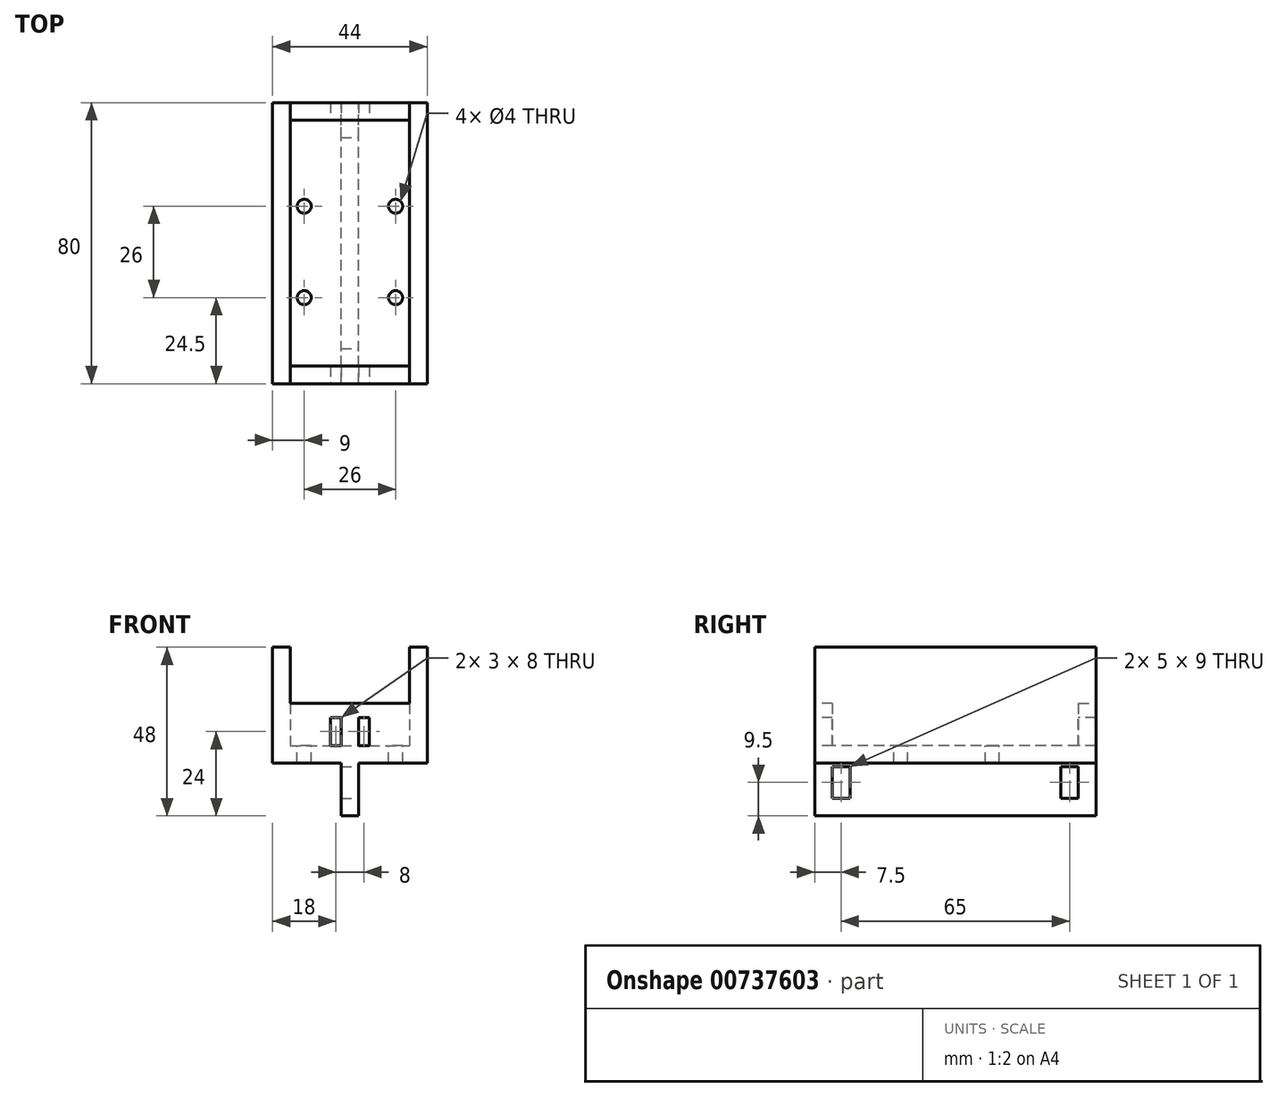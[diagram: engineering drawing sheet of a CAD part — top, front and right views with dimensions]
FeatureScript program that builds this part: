
annotation { "Feature Type Name" : "Feature", "Feature Type Description" : "" }
export const myFeature = defineFeature(function(context is Context, id is Id, definition is map)
    precondition{}
    {
        {
            var Q0;
            Q0=qCreatedBy(makeId("Top.planeOp"),FACE);
            var sketch = newSketch(context, id + "F0", { "sketchPlane" : qUnion([Q0])});
            skLineSegment(sketch, "E0.bottom", {"start": v(-13, 13) * mm, "end": v(13, 13) * mm, "construction": true});
            skLineSegment(sketch, "E0.top", {"start": v(-13, -13) * mm, "end": v(13, -13) * mm, "construction": true});
            skLineSegment(sketch, "E0.left", {"start": v(-13, 13) * mm, "end": v(-13, -13) * mm, "construction": true});
            skLineSegment(sketch, "E0.right", {"start": v(13, 13) * mm, "end": v(13, -13) * mm, "construction": true});
            skPoint(sketch, "E0.middle", {"position": v(0, 0) * mm});
            skCircle(sketch, "E1", {"center": v(-13, 13) * mm, "radius": 2 * mm});
            skCircle(sketch, "E2", {"center": v(13, 13) * mm, "radius": 2 * mm});
            skCircle(sketch, "E3", {"center": v(13, -13) * mm, "radius": 2 * mm});
            skCircle(sketch, "E4", {"center": v(-13, -13) * mm, "radius": 2 * mm});
            skLineSegment(sketch, "E5.bottom", {"start": v(-22, 37.5) * mm, "end": v(22, 37.5) * mm});
            skLineSegment(sketch, "E5.top", {"start": v(-22, -37.5) * mm, "end": v(22, -37.5) * mm});
            skLineSegment(sketch, "E5.left", {"start": v(-22, 37.5) * mm, "end": v(-22, -37.5) * mm});
            skLineSegment(sketch, "E5.right", {"start": v(22, 37.5) * mm, "end": v(22, -37.5) * mm});
            skLineSegment(sketch, "E6", {"start": v(-17, 37.5) * mm, "end": v(-17, -37.5) * mm});
            skLineSegment(sketch, "E7.MirrorCS", {"start": v(17, 37.5) * mm, "end": v(17, -37.5) * mm});
            skLineSegment(sketch, "E8", {"start": v(-17, -32.5) * mm, "end": v(17, -32.5) * mm});
            skLineSegment(sketch, "E9", {"start": v(22, 37.5) * mm, "end": v(22, 42.5) * mm});
            skLineSegment(sketch, "E10", {"start": v(22, 42.5) * mm, "end": v(-22, 42.5) * mm});
            skLineSegment(sketch, "E11", {"start": v(-22, 42.5) * mm, "end": v(-22, 37.5) * mm});
            skLineSegment(sketch, "E12", {"start": v(17, 37.5) * mm, "end": v(17, 42.5) * mm});
            skLineSegment(sketch, "E13", {"start": v(-17, 37.5) * mm, "end": v(-17, 42.5) * mm});
            skSolve(sketch);
        }
        {
            var Q0;
            {var subQ0=sQuery(id+"F0.wireOp",EDGE,"E5.left");Q0=makeQuery(id+"F0.imprint","IMPRINT",FACE,{"disambiguationData":[TD([[makeQuery(id+"F0.imprint","IMPRINT",EDGE,{"derivedFrom":subQ0}),1.0]])]});}
            var Q1;
            {var subQ0=sQuery(id+"F0.wireOp",EDGE,"E5.right");Q1=makeQuery(id+"F0.imprint","IMPRINT",FACE,{"disambiguationData":[TD([[makeQuery(id+"F0.imprint","IMPRINT",EDGE,{"derivedFrom":subQ0}),-1.0]])]});}
            extrude(context, id + "F1", {"entities" : qUnion([Q0, Q1]), "depth" : 28 * mm, "offsetDistance" : 25 * mm});
        }
        {
            var Q0;
            {var subQ0=sQuery(id+"F0.wireOp",EDGE,"E5.left");Q0=makeQuery(id+"F0.imprint","IMPRINT",FACE,{"disambiguationData":[TD([[makeQuery(id+"F0.imprint","IMPRINT",EDGE,{"derivedFrom":subQ0}),1.0]])]});}
            var Q1;
            Q1=makeQuery(id+"F0.imprint","IMPRINT",FACE,{"disambiguationData":[TD([[makeQuery(id+"F0.imprint","IMPRINT",EDGE,{"derivedFrom":sQuery(id+"F0.wireOp",EDGE,"E1")}),-1.0]])]});
            var Q2;
            {var subQ0=sQuery(id+"F0.wireOp",EDGE,"E5.right");Q2=makeQuery(id+"F0.imprint","IMPRINT",FACE,{"disambiguationData":[TD([[makeQuery(id+"F0.imprint","IMPRINT",EDGE,{"derivedFrom":subQ0}),-1.0]])]});}
            var Q3;
            {var subQ5=sQuery(id+"F0.wireOp",EDGE,"E8");Q3=makeQuery(id+"F0.imprint","IMPRINT",FACE,{"disambiguationData":[TD([[makeQuery(id+"F0.imprint","IMPRINT",EDGE,{"derivedFrom":subQ5}),-1.0]])]});}
            extrude(context, id + "F2", {"entities" : qUnion([Q0, Q1, Q2, Q3]), "operationType" : NewBodyOperationType.ADD, "oppositeDirection" : true, "depth" : 5 * mm, "offsetDistance" : 25 * mm});
        }
        {
            var Q0;
            {var subQ5=sQuery(id+"F0.wireOp",EDGE,"E8");Q0=makeQuery(id+"F0.imprint","IMPRINT",FACE,{"disambiguationData":[TD([[makeQuery(id+"F0.imprint","IMPRINT",EDGE,{"derivedFrom":subQ5}),-1.0]])]});}
            var Q1;
            Q1=makeQuery(id+"F1.opExtrude","CAP_FACE",FACE,{"disambiguationData":[OSD([sQuery(id+"F0.wireOp",EDGE,"E5.bottom"),sQuery(id+"F0.wireOp",EDGE,"E5.top"),sQuery(id+"F0.wireOp",EDGE,"E5.left"),sQuery(id+"F0.wireOp",EDGE,"E6")])],"isStart":false});
            extrude(context, id + "F3", {"entities" : qUnion([Q0]), "operationType" : NewBodyOperationType.ADD, "depth" : 12 * mm, "endBoundEntityFace" : qUnion([Q1]), "offsetDistance" : 25 * mm});
        }
        {
            var Q0;
            {var subQ0=sQuery(id+"F0.wireOp",EDGE,"E9");Q0=makeQuery(id+"F0.imprint","IMPRINT",FACE,{"disambiguationData":[TD([[makeQuery(id+"F0.imprint","IMPRINT",EDGE,{"derivedFrom":subQ0}),1.0]])]});}
            var Q1;
            {var subQ2=sQuery(id+"F0.wireOp",EDGE,"E12");Q1=makeQuery(id+"F0.imprint","IMPRINT",FACE,{"disambiguationData":[TD([[makeQuery(id+"F0.imprint","IMPRINT",EDGE,{"derivedFrom":subQ2}),1.0]])]});}
            var Q2;
            {var subQ0=sQuery(id+"F0.wireOp",EDGE,"E11");Q2=makeQuery(id+"F0.imprint","IMPRINT",FACE,{"disambiguationData":[TD([[makeQuery(id+"F0.imprint","IMPRINT",EDGE,{"derivedFrom":subQ0}),1.0]])]});}
            var Q3;
            Q3=makeQuery(id+"F2.opExtrude","CAP_FACE",FACE,{"disambiguationData":[OSD([sQuery(id+"F0.wireOp",EDGE,"E1"),sQuery(id+"F0.wireOp",EDGE,"E2"),sQuery(id+"F0.wireOp",EDGE,"E3"),sQuery(id+"F0.wireOp",EDGE,"E4"),sQuery(id+"F0.wireOp",EDGE,"E5.bottom"),sQuery(id+"F0.wireOp",EDGE,"E5.top"),sQuery(id+"F0.wireOp",EDGE,"E5.left"),sQuery(id+"F0.wireOp",EDGE,"E5.right")])],"isStart":false});
            extrude(context, id + "F4", {"entities" : qUnion([Q0, Q1, Q2]), "operationType" : NewBodyOperationType.ADD, "endBound" : BoundingType.UP_TO_SURFACE, "oppositeDirection" : true, "depth" : 25 * mm, "endBoundEntityFace" : qUnion([Q3]), "offsetDistance" : 25 * mm});
        }
        {
            var Q0;
            {var subQ0=sQuery(id+"F0.wireOp",EDGE,"E9");Q0=makeQuery(id+"F0.imprint","IMPRINT",FACE,{"disambiguationData":[TD([[makeQuery(id+"F0.imprint","IMPRINT",EDGE,{"derivedFrom":subQ0}),1.0]])]});}
            var Q1;
            {var subQ0=sQuery(id+"F0.wireOp",EDGE,"E11");Q1=makeQuery(id+"F0.imprint","IMPRINT",FACE,{"disambiguationData":[TD([[makeQuery(id+"F0.imprint","IMPRINT",EDGE,{"derivedFrom":subQ0}),1.0]])]});}
            var Q2;
            Q2=makeQuery(id+"F1.opExtrude","CAP_FACE",FACE,{"disambiguationData":[OSD([sQuery(id+"F0.wireOp",EDGE,"E5.bottom"),sQuery(id+"F0.wireOp",EDGE,"E5.top"),sQuery(id+"F0.wireOp",EDGE,"E5.right"),sQuery(id+"F0.wireOp",EDGE,"E7.MirrorCS")])],"isStart":false});
            extrude(context, id + "F5", {"entities" : qUnion([Q0, Q1]), "operationType" : NewBodyOperationType.ADD, "endBound" : BoundingType.UP_TO_SURFACE, "depth" : 25 * mm, "endBoundEntityFace" : qUnion([Q2]), "offsetDistance" : 25 * mm});
        }
        {
            var Q0;
            {var subQ2=sQuery(id+"F0.wireOp",EDGE,"E12");Q0=makeQuery(id+"F0.imprint","IMPRINT",FACE,{"disambiguationData":[TD([[makeQuery(id+"F0.imprint","IMPRINT",EDGE,{"derivedFrom":subQ2}),1.0]])]});}
            extrude(context, id + "F6", {"entities" : qUnion([Q0]), "operationType" : NewBodyOperationType.ADD, "depth" : 12 * mm, "offsetDistance" : 25 * mm});
        }
        {
            var Q0;
            {var subQ0=sQuery(id+"F0.wireOp",EDGE,"E5.right");var subQ1=sQuery(id+"F0.wireOp",EDGE,"E5.left");var subQ2=sQuery(id+"F0.wireOp",EDGE,"E5.top");var subQ3=sQuery(id+"F0.wireOp",EDGE,"E5.bottom");var subQ4=sQuery(id+"F0.wireOp",EDGE,"E4");var subQ5=sQuery(id+"F0.wireOp",EDGE,"E3");var subQ6=sQuery(id+"F0.wireOp",EDGE,"E2");var subQ7=sQuery(id+"F0.wireOp",EDGE,"E1");Q0=makeQuery(id+"F4.boolean.opBoolean","MERGE",FACE,{"derivedFrom":[makeQuery(id+"F2.opExtrude","CAP_FACE",FACE,{"disambiguationData":[OSD([subQ7,subQ6,subQ5,subQ4,subQ3,subQ2,subQ1,subQ0])],"isStart":false}),makeQuery(id+"F4.opExtrude","CAP_FACE",FACE,{"disambiguationData":[OSD([subQ7,subQ6,subQ5,subQ4,subQ3,subQ2,subQ1,subQ0])],"isStart":false})]});}
            var sketch = newSketch(context, id + "F7", { "sketchPlane" : qUnion([Q0])});
            skLineSegment(sketch, "E14", {"start": v(-2.5, 37.5) * mm, "end": v(-2.5, -42.5) * mm});
            skLineSegment(sketch, "E15", {"start": v(2.5, 37.5) * mm, "end": v(2.5, -42.5) * mm});
            skSolve(sketch);
        }
        {
            var Q0;
            {var subQ0=sQuery(id+"F7.wireOp",EDGE,"E14");Q0=makeQuery(id+"F7.imprint","IMPRINT",FACE,{"disambiguationData":[TD([[makeQuery(id+"F7.imprint","IMPRINT",EDGE,{"derivedFrom":subQ0}),1.0]])]});}
            extrude(context, id + "F8", {"entities" : qUnion([Q0]), "operationType" : NewBodyOperationType.ADD, "depth" : 15 * mm, "offsetDistance" : 25 * mm});
        }
        {
            var Q0;
            Q0=makeQuery(id+"F8.opExtrude","SWEPT_FACE",FACE,{"disambiguationData":[OSD([sQuery(id+"F7.wireOp",EDGE,"E15")])]});
            var sketch = newSketch(context, id + "F9", { "sketchPlane" : qUnion([Q0])});
            skLineSegment(sketch, "E16.bottom", {"start": v(-32.5, -15) * mm, "end": v(-27.5, -15) * mm});
            skLineSegment(sketch, "E16.top", {"start": v(-32.5, -6) * mm, "end": v(-27.5, -6) * mm});
            skLineSegment(sketch, "E16.left", {"start": v(-32.5, -15) * mm, "end": v(-32.5, -6) * mm});
            skLineSegment(sketch, "E16.right", {"start": v(-27.5, -15) * mm, "end": v(-27.5, -6) * mm});
            skLineSegment(sketch, "E17.bottom", {"start": v(32.5, -6) * mm, "end": v(37.5, -6) * mm});
            skLineSegment(sketch, "E17.top", {"start": v(32.5, -15) * mm, "end": v(37.5, -15) * mm});
            skLineSegment(sketch, "E17.left", {"start": v(32.5, -6) * mm, "end": v(32.5, -15) * mm});
            skLineSegment(sketch, "E17.right", {"start": v(37.5, -6) * mm, "end": v(37.5, -15) * mm});
            skSolve(sketch);
        }
        {
            var Q0;
            Q0=makeQuery(id+"F9.imprint","IMPRINT",FACE,{"disambiguationData":[TD([[makeQuery(id+"F9.imprint","IMPRINT",EDGE,{"derivedFrom":sQuery(id+"F9.wireOp",EDGE,"E16.bottom")}),1.0]])]});
            extrude(context, id + "F10", {"entities" : qUnion([Q0]), "operationType" : NewBodyOperationType.REMOVE, "endBound" : BoundingType.THROUGH_ALL, "oppositeDirection" : true, "depth" : 25 * mm, "offsetDistance" : 25 * mm});
        }
        {
            var Q0;
            {var subQ0=sQuery(id+"F0.wireOp",EDGE,"E5.top");Q0=makeQuery(id+"F8.boolean.opBoolean","MERGE",FACE,{"derivedFrom":[makeQuery(id+"F3.boolean.opBoolean","MERGE",FACE,{"derivedFrom":[makeQuery(id+"F2.boolean.opBoolean","MERGE",FACE,{"derivedFrom":[makeQuery(id+"F1.opExtrude","SWEPT_FACE",FACE,{"disambiguationData":[OSD([subQ0]),TDD([makeQuery(id+"F0.imprint","IMPRINT",EDGE,{"disambiguationData":[TD([[makeQuery(id+"F0.imprint","INTERSECT",VERTEX,{"derivedFrom":[subQ0,sQuery(id+"F0.wireOp",EDGE,"E5.left")]}),-1.0]])],"derivedFrom":subQ0})])]}),makeQuery(id+"F1.opExtrude","SWEPT_FACE",FACE,{"disambiguationData":[OSD([subQ0]),TDD([makeQuery(id+"F0.imprint","IMPRINT",EDGE,{"disambiguationData":[TD([[makeQuery(id+"F0.imprint","INTERSECT",VERTEX,{"derivedFrom":[subQ0,sQuery(id+"F0.wireOp",EDGE,"E5.right")]}),1.0]])],"derivedFrom":subQ0})])]}),makeQuery(id+"F2.opExtrude","SWEPT_FACE",FACE,{"disambiguationData":[OSD([subQ0])]})]}),makeQuery(id+"F3.opExtrude","SWEPT_FACE",FACE,{"disambiguationData":[OSD([subQ0])]})]}),makeQuery(id+"F8.opExtrude","SWEPT_FACE",FACE,{"disambiguationData":[OSD([subQ0])]})]});}
            var sketch = newSketch(context, id + "F11", { "sketchPlane" : qUnion([Q0])});
            skLineSegment(sketch, "E18.bottom", {"start": v(-2.5, 8) * mm, "end": v(2.5, 8) * mm});
            skLineSegment(sketch, "E18.top", {"start": v(-2.5, 0) * mm, "end": v(2.5, 0) * mm});
            skLineSegment(sketch, "E18.left", {"start": v(-2.5, 8) * mm, "end": v(-2.5, 0) * mm});
            skLineSegment(sketch, "E18.right", {"start": v(2.5, 8) * mm, "end": v(2.5, 0) * mm});
            skLineSegment(sketch, "E19", {"start": v(-2.5, 0) * mm, "end": v(-5.5, 0) * mm});
            skLineSegment(sketch, "E20", {"start": v(-5.5, 0) * mm, "end": v(-5.5, 8) * mm});
            skLineSegment(sketch, "E21", {"start": v(-5.5, 8) * mm, "end": v(-2.5, 8) * mm});
            skLineSegment(sketch, "E22", {"start": v(2.5, 8) * mm, "end": v(5.5, 8) * mm});
            skLineSegment(sketch, "E23", {"start": v(5.5, 8) * mm, "end": v(5.5, 0) * mm});
            skLineSegment(sketch, "E24", {"start": v(5.5, 0) * mm, "end": v(2.5, 0) * mm});
            skSolve(sketch);
        }
        {
            var Q0;
            Q0=makeQuery(id+"F11.imprint","IMPRINT",FACE,{"disambiguationData":[TD([[makeQuery(id+"F11.imprint","IMPRINT",EDGE,{"derivedFrom":sQuery(id+"F11.wireOp",EDGE,"E18.left")}),-1.0]])]});
            var Q1;
            Q1=makeQuery(id+"F11.imprint","IMPRINT",FACE,{"disambiguationData":[TD([[makeQuery(id+"F11.imprint","IMPRINT",EDGE,{"derivedFrom":sQuery(id+"F11.wireOp",EDGE,"E18.right")}),1.0]])]});
            extrude(context, id + "F12", {"entities" : qUnion([Q0, Q1]), "operationType" : NewBodyOperationType.REMOVE, "endBound" : BoundingType.THROUGH_ALL, "oppositeDirection" : true, "depth" : 25 * mm, "offsetDistance" : 25 * mm});
        }
        {
            var Q0;
            Q0=makeQuery(id+"F9.imprint","IMPRINT",FACE,{"disambiguationData":[TD([[makeQuery(id+"F9.imprint","IMPRINT",EDGE,{"derivedFrom":sQuery(id+"F9.wireOp",EDGE,"E17.bottom")}),-1.0]])]});
            extrude(context, id + "F13", {"entities" : qUnion([Q0]), "operationType" : NewBodyOperationType.REMOVE, "endBound" : BoundingType.THROUGH_ALL, "oppositeDirection" : true, "depth" : 25 * mm, "offsetDistance" : 25 * mm});
        }
    });
